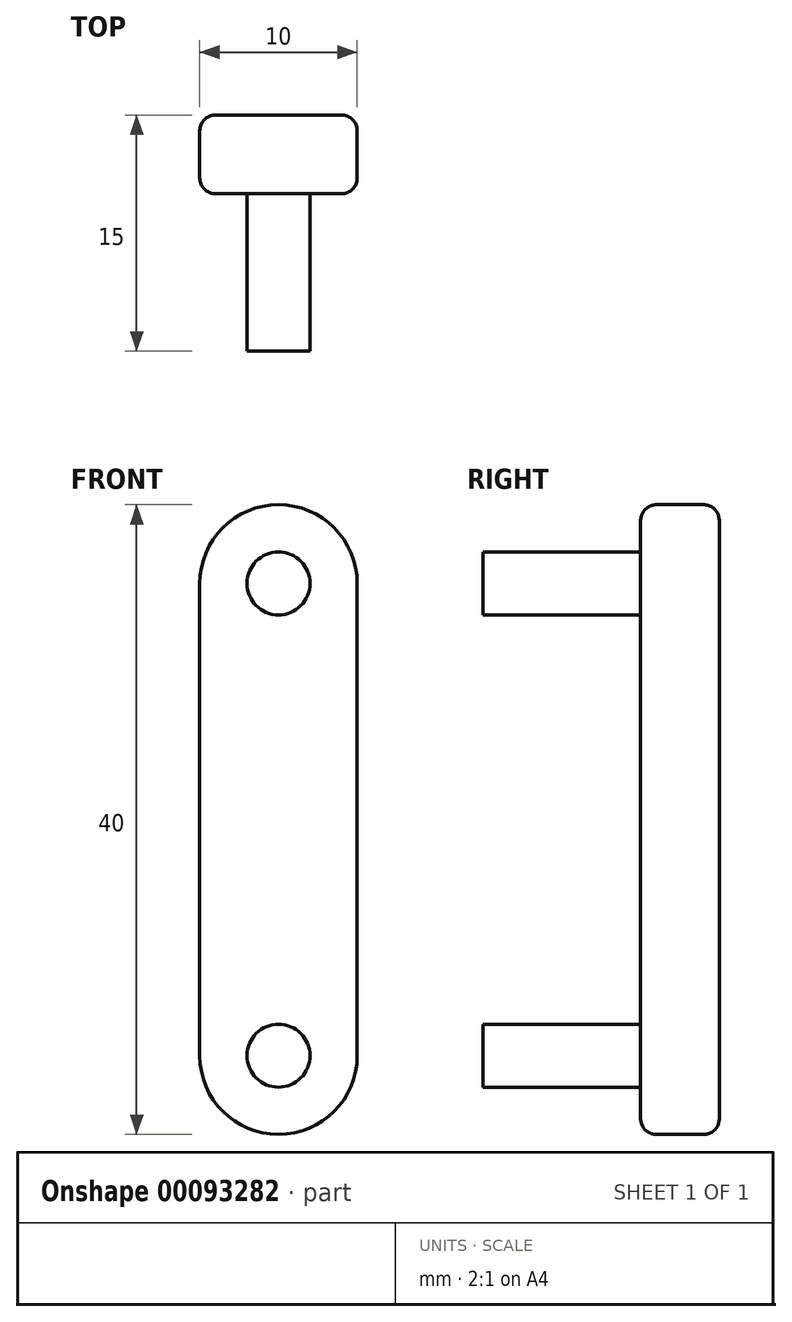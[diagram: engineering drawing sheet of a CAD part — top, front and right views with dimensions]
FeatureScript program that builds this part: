
annotation { "Feature Type Name" : "Feature", "Feature Type Description" : "" }
export const myFeature = defineFeature(function(context is Context, id is Id, definition is map)
    precondition{}
    {
        {
            var Q0;
            Q0=qCreatedBy(makeId("Front.planeOp"),FACE);
            var sketch = newSketch(context, id + "F0", { "sketchPlane" : qUnion([Q0])});
            skLineSegment(sketch, "E0.bottom", {"start": v(-5, 15) * mm, "end": v(5, 15) * mm});
            skLineSegment(sketch, "E0.top", {"start": v(-5, -15) * mm, "end": v(5, -15) * mm});
            skLineSegment(sketch, "E0.left", {"start": v(-5, 15) * mm, "end": v(-5, -15) * mm});
            skLineSegment(sketch, "E0.right", {"start": v(5, 15) * mm, "end": v(5, -15) * mm});
            skPoint(sketch, "E0.middle", {"position": v(0, 0) * mm});
            skArc(sketch, "E1", {"start": v(-5, 15) * mm, "mid": v(0, 20) * mm, "end": v(5, 15) * mm});
            skArc(sketch, "E2", {"start": v(-5, -15) * mm, "mid": v(0, -20) * mm, "end": v(5, -15) * mm});
            skSolve(sketch);
        }
        {
            var Q0;
            Q0=makeQuery(id+"F0.imprint","IMPRINT",FACE,{"disambiguationData":[TD([[makeQuery(id+"F0.imprint","IMPRINT",EDGE,{"derivedFrom":sQuery(id+"F0.wireOp",EDGE,"E0.top")}),-1.0]])]});
            var Q1;
            Q1=makeQuery(id+"F0.imprint","IMPRINT",FACE,{"disambiguationData":[TD([[makeQuery(id+"F0.imprint","IMPRINT",EDGE,{"derivedFrom":sQuery(id+"F0.wireOp",EDGE,"E0.bottom")}),1.0]])]});
            var Q2;
            Q2=makeQuery(id+"F0.imprint","IMPRINT",FACE,{"disambiguationData":[TD([[makeQuery(id+"F0.imprint","IMPRINT",EDGE,{"derivedFrom":sQuery(id+"F0.wireOp",EDGE,"E0.bottom")}),-1.0]])]});
            extrude(context, id + "F1", {"entities" : qUnion([Q0, Q1, Q2]), "depth" : 5 * mm});
        }
        {
            var Q0;
            Q0=qCreatedBy(makeId("Front.planeOp"),FACE);
            var sketch = newSketch(context, id + "F2", { "sketchPlane" : qUnion([Q0])});
            skLineSegment(sketch, "E3", {"start": v(7.52, 15) * mm, "end": v(-10.58, 15) * mm});
            skLineSegment(sketch, "E4", {"start": v(6.14, -15) * mm, "end": v(-13.84, -15) * mm});
            skCircle(sketch, "E5", {"center": v(0, 15) * mm, "radius": 2 * mm});
            skPoint(sketch, "E5.centerSnap0", {"position": v(-1.53, 15) * mm});
            skCircle(sketch, "E6", {"center": v(0, -15) * mm, "radius": 2 * mm});
            skSolve(sketch);
        }
        {
            var Q0;
            Q0=sQuery(id+"F2.wireOp",VERTEX,"E5.center");
            var Q1;
            Q1=sQuery(id+"F2.wireOp",VERTEX,"E6.center");
            var Q2;
            Q2=makeQuery(id+"F1.opExtrude","SWEPT_BODY",BODY,{"disambiguationData":[OSD([sQuery(id+"F0.wireOp",EDGE,"E0.left"),sQuery(id+"F0.wireOp",EDGE,"E0.right"),sQuery(id+"F0.wireOp",EDGE,"E1"),sQuery(id+"F0.wireOp",EDGE,"E2")])]});
            hole(context, id + "F3", {"style" : HoleStyle.SIMPLE, "endStyle" : HoleEndStyle.THROUGH, "oppositeDirection" : true, "holeDiameter" : 4 * mm, "locations" : qUnion([Q0, Q1]), "scope" : qUnion([Q2]), "isTappedThrough" : true});
        }
        {
            var Q0;
            Q0=makeQuery(id+"F1.opExtrude","CAP_EDGE",EDGE,{"disambiguationData":[OSD([sQuery(id+"F0.wireOp",EDGE,"E0.right")])],"isStart":false});
            var Q1;
            Q1=makeQuery(id+"F1.opExtrude","CAP_EDGE",EDGE,{"disambiguationData":[OSD([sQuery(id+"F0.wireOp",EDGE,"E0.right")])],"isStart":true});
            fillet(context, id + "F4", {"entities" : qUnion([Q0, Q1]), "radius" : 1 * mm, "tangentPropagation" : true, "allowEdgeOverflow" : false});
        }
        {
            var Q0;
            {var subQ0=sQuery(id+"F2.wireOp",EDGE,"E5");var subQ1=sQuery(id+"F2.wireOp",EDGE,"E3");var subQ2=makeQuery(id+"F2.imprint","INTERSECT",VERTEX,{"disambiguationData":[OD(0.0)],"derivedFrom":[subQ1,subQ0]});Q0=makeQuery(id+"F2.imprint","IMPRINT",FACE,{"disambiguationData":[TD([[makeQuery(id+"F2.imprint","IMPRINT",EDGE,{"disambiguationData":[TD([[subQ2,1.0]])],"derivedFrom":subQ1}),1.0]])]});}
            var Q1;
            {var subQ0=sQuery(id+"F2.wireOp",EDGE,"E5");var subQ1=sQuery(id+"F2.wireOp",EDGE,"E3");var subQ2=makeQuery(id+"F2.imprint","INTERSECT",VERTEX,{"disambiguationData":[OD(0.0)],"derivedFrom":[subQ1,subQ0]});Q1=makeQuery(id+"F2.imprint","IMPRINT",FACE,{"disambiguationData":[TD([[makeQuery(id+"F2.imprint","IMPRINT",EDGE,{"disambiguationData":[TD([[subQ2,1.0]])],"derivedFrom":subQ1}),-1.0]])]});}
            var Q2;
            {var subQ0=sQuery(id+"F2.wireOp",EDGE,"E6");var subQ1=sQuery(id+"F2.wireOp",EDGE,"E4");var subQ2=makeQuery(id+"F2.imprint","INTERSECT",VERTEX,{"disambiguationData":[OD(0.0)],"derivedFrom":[subQ1,subQ0]});Q2=makeQuery(id+"F2.imprint","IMPRINT",FACE,{"disambiguationData":[TD([[makeQuery(id+"F2.imprint","IMPRINT",EDGE,{"disambiguationData":[TD([[subQ2,1.0]])],"derivedFrom":subQ1}),1.0]])]});}
            var Q3;
            {var subQ0=sQuery(id+"F2.wireOp",EDGE,"E6");var subQ1=sQuery(id+"F2.wireOp",EDGE,"E4");var subQ2=makeQuery(id+"F2.imprint","INTERSECT",VERTEX,{"disambiguationData":[OD(0.0)],"derivedFrom":[subQ1,subQ0]});Q3=makeQuery(id+"F2.imprint","IMPRINT",FACE,{"disambiguationData":[TD([[makeQuery(id+"F2.imprint","IMPRINT",EDGE,{"disambiguationData":[TD([[subQ2,1.0]])],"derivedFrom":subQ1}),-1.0]])]});}
            extrude(context, id + "F5", {"entities" : qUnion([Q0, Q1, Q2, Q3]), "operationType" : NewBodyOperationType.ADD, "depth" : 15 * mm});
        }
    });
